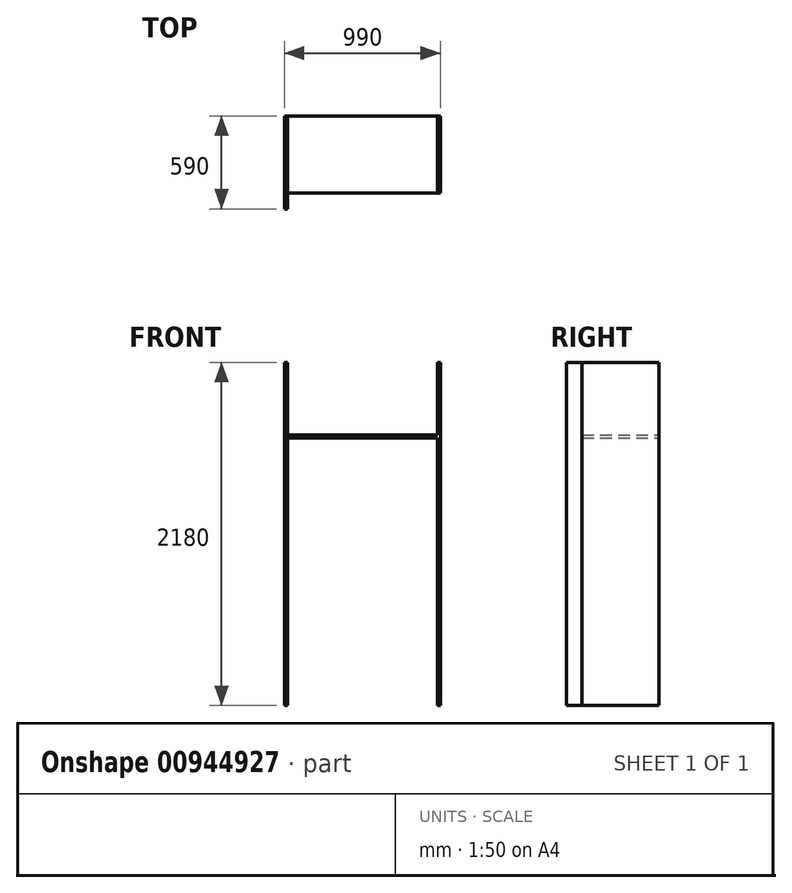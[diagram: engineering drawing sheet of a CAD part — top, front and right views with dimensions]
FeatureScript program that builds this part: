
annotation { "Feature Type Name" : "Feature", "Feature Type Description" : "" }
export const myFeature = defineFeature(function(context is Context, id is Id, definition is map)
    precondition{}
    {
        {
            var Q0;
            Q0=qCreatedBy(makeId("Front.planeOp"),FACE);
            var sketch = newSketch(context, id + "F0", { "sketchPlane" : qUnion([Q0])});
            skLineSegment(sketch, "E0.bottom", {"start": v(0, 0) * mm, "end": v(18, 0) * mm});
            skLineSegment(sketch, "E0.left", {"start": v(0, 0) * mm, "end": v(0, 2180) * mm});
            skLineSegment(sketch, "E0.right", {"start": v(990, 0) * mm, "end": v(990, 2180) * mm});
            skLineSegment(sketch, "E1.0", {"start": v(972, 0) * mm, "end": v(972, 1700) * mm});
            skLineSegment(sketch, "E1.2", {"start": v(18, 0) * mm, "end": v(18, 1700) * mm});
            skLineSegment(sketch, "E2.trimOffspring", {"start": v(972, 0) * mm, "end": v(990, 0) * mm});
            skLineSegment(sketch, "E3.bottom", {"start": v(18, 1700) * mm, "end": v(972, 1700) * mm});
            skLineSegment(sketch, "E3.top", {"start": v(18, 1718) * mm, "end": v(972, 1718) * mm});
            skLineSegment(sketch, "E4.trimOffspring", {"start": v(18, 1718) * mm, "end": v(18, 2162) * mm});
            skLineSegment(sketch, "E5.trimOffspring", {"start": v(972, 1718) * mm, "end": v(972, 2162) * mm});
            skLineSegment(sketch, "E6", {"start": v(0, 2180) * mm, "end": v(18, 2180) * mm});
            skLineSegment(sketch, "E7", {"start": v(18, 2180) * mm, "end": v(18, 2162) * mm});
            skLineSegment(sketch, "E8", {"start": v(972, 2162) * mm, "end": v(972, 2180) * mm});
            skLineSegment(sketch, "E9", {"start": v(972, 2180) * mm, "end": v(990, 2180) * mm});
            skSolve(sketch);
        }
        {
            var Q0;
            Q0 = qSketchRegion(id + "F0", true);
            extrude(context, id + "F1", {"entities" : qUnion([Q0]), "depth" : 490 * mm, "offsetDistance" : 25 * mm});
        }
        {
            var Q0;
            Q0=makeQuery(id+"F1.opExtrude","SWEPT_FACE",FACE,{"disambiguationData":[OSD([sQuery(id+"F0.wireOp",EDGE,"E0.left")])]});
            var sketch = newSketch(context, id + "F2", { "sketchPlane" : qUnion([Q0])});
            skLineSegment(sketch, "E10.bottom", {"start": v(490, 0) * mm, "end": v(590, 0) * mm});
            skLineSegment(sketch, "E10.top", {"start": v(490, 2180) * mm, "end": v(590, 2180) * mm});
            skLineSegment(sketch, "E10.left", {"start": v(490, 0) * mm, "end": v(490, 2180) * mm});
            skLineSegment(sketch, "E10.right", {"start": v(590, 0) * mm, "end": v(590, 2180) * mm});
            skSolve(sketch);
        }
        {
            var Q0;
            Q0 = qSketchRegion(id + "F2", true);
            extrude(context, id + "F3", {"entities" : qUnion([Q0]), "operationType" : NewBodyOperationType.ADD, "oppositeDirection" : true, "depth" : 18 * mm, "offsetDistance" : 25 * mm});
        }
    });
